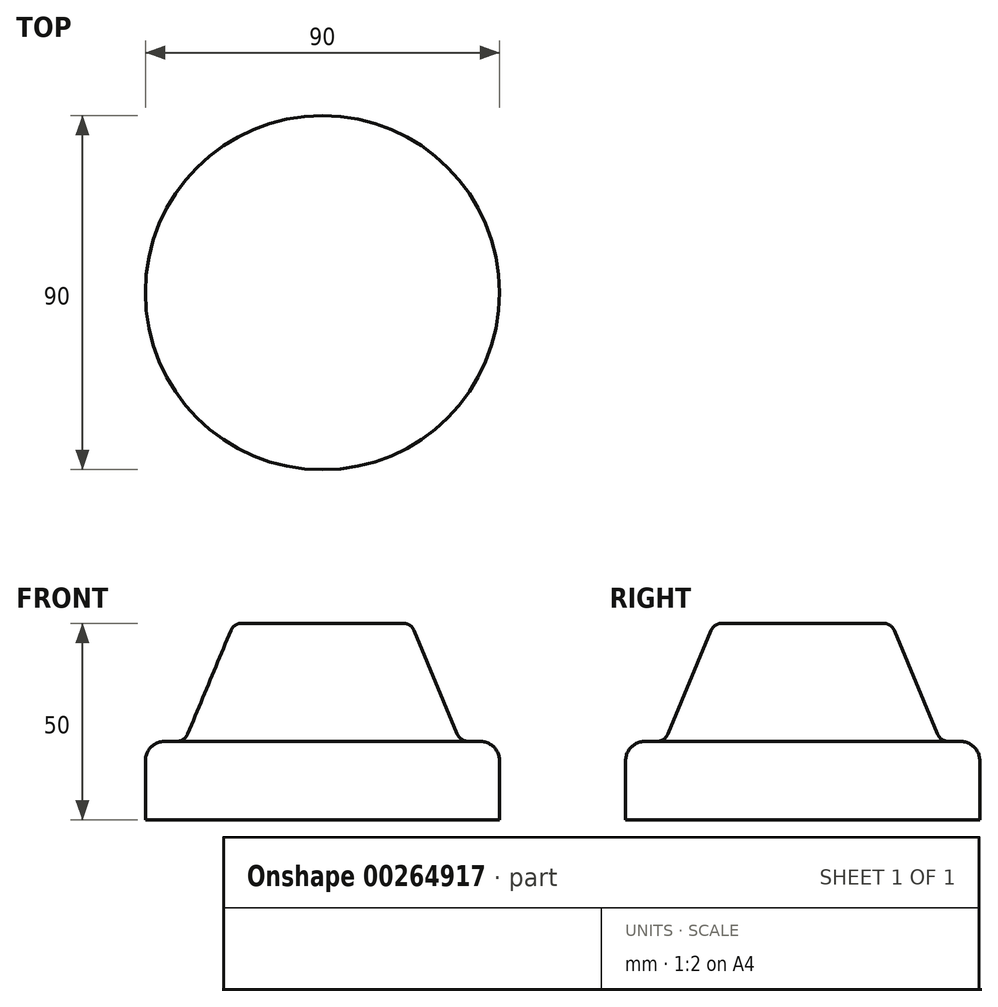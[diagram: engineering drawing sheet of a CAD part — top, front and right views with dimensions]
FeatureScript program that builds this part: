
annotation { "Feature Type Name" : "Feature", "Feature Type Description" : "" }
export const myFeature = defineFeature(function(context is Context, id is Id, definition is map)
    precondition{}
    {
        {
            var Q0;
            Q0=qCreatedBy(makeId("Front.planeOp"),FACE);
            var sketch = newSketch(context, id + "F0", { "sketchPlane" : qUnion([Q0])});
            skLineSegment(sketch, "E0", {"start": v(0, 50) * mm, "end": v(0, 0) * mm});
            skLineSegment(sketch, "E1", {"start": v(0, 0) * mm, "end": v(45, 0) * mm});
            skLineSegment(sketch, "E2", {"start": v(45, 0) * mm, "end": v(45, 15) * mm});
            skLineSegment(sketch, "E3", {"start": v(40, 20) * mm, "end": v(37, 20) * mm});
            skLineSegment(sketch, "E4", {"start": v(34.23, 21.85) * mm, "end": v(23.27, 48.15) * mm});
            skLineSegment(sketch, "E5", {"start": v(20.5, 50) * mm, "end": v(0, 50) * mm});
            skPoint(sketch, "E6.visualSharp", {"position": v(22.5, 50) * mm});
            skArc(sketch, "E6.filletArc", {"start": v(23.27, 48.15) * mm, "mid": v(22.16, 49.5) * mm, "end": v(20.5, 50) * mm});
            skPoint(sketch, "E7.visualSharp", {"position": v(35, 20) * mm});
            skArc(sketch, "E7.filletArc", {"start": v(34.23, 21.85) * mm, "mid": v(35.34, 20.5) * mm, "end": v(37, 20) * mm});
            skPoint(sketch, "E8.visualSharp", {"position": v(45, 20) * mm});
            skArc(sketch, "E8.filletArc", {"start": v(45, 15) * mm, "mid": v(43.54, 18.54) * mm, "end": v(40, 20) * mm});
            skLineSegment(sketch, "E9", {"start": v(0, -22) * mm, "end": v(0, 69.76) * mm});
            skLineSegment(sketch, "E10", {"start": v(0, 69.76) * mm, "end": v(0, -13.63) * mm, "construction": true});
            skSolve(sketch);
        }
        {
            var Q0;
            {var subQ1=sQuery(id+"F0.wireOp",EDGE,"E1");Q0=makeQuery(id+"F0.imprint","IMPRINT",FACE,{"disambiguationData":[TD([[makeQuery(id+"F0.imprint","IMPRINT",EDGE,{"derivedFrom":subQ1}),1.0]])]});}
            var Q1;
            Q1=sQuery(id+"F0.wireOp",EDGE,"E9");
            revolve(context, id + "F1", {"entities" : qUnion([Q0]), "axis" : qUnion([Q1]), "revolveType" : RevolveType.FULL});
        }
    });
